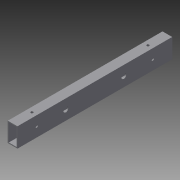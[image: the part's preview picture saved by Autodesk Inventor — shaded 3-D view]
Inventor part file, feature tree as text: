
AUTODESK INVENTOR PART (.ipt)
format: ipt  version: 2015 (Build 190159000, 159)  size: 114,176 bytes
history: native  units: in
note: dims shown in document units (in); Inventor stores cm internally (conversion verified against a paired STEP export)
features: sketch x4, hole x3, extrude x1, projected_geometry x1
ambient origin geometry x8: Origin, YZ Plane, XZ Plane, XY Plane, X Axis, Y Axis, Z Axis, Center Point
bodies: Solid1 (feature_tree)
feature tree (9):
  extrude  "Extrusion1"  Depth=0.5in
  hole  "Hole1"  [1 undecoded]
  hole  "Hole2"  [1 undecoded]
  hole  "Hole3"  [1 undecoded]
  sketch  "Sketch1"  dims[d0=1.0in d1=0.5in]
  sketch  "Sketch2"  dims[d2=0.05in d3=8.0in d4=0.0in]
  sketch  "Sketch3"  dims[d5=0.5in d6=1.0in]
  sketch  "Sketch4"  dims[d7=1.0in d11=0.1285in d12=0.75in d13=0.375in d14=0.25in d15=0.5635in d16=1.0in d17=0.8108in d18=1.5in d19=1.5in d20=0.257in d21=0.75in d22=0.375in d23=0.25in d24=0.5635in d25=1.0in d26=0.8108in d27=0.25in d28=1.0in d29=1.0in d30=0.128in d31=0.75in d32=0.375in d33=0.25in d34=0.5635in d35=1.0in d36=0.8108in]
  projected_geometry  "Projected Loop1"
note: 3 required parameter values undecoded (feature->parameter linkage not recoverable at this tier; creation-order binding heuristic only, values carry confidence <= 0.55)
